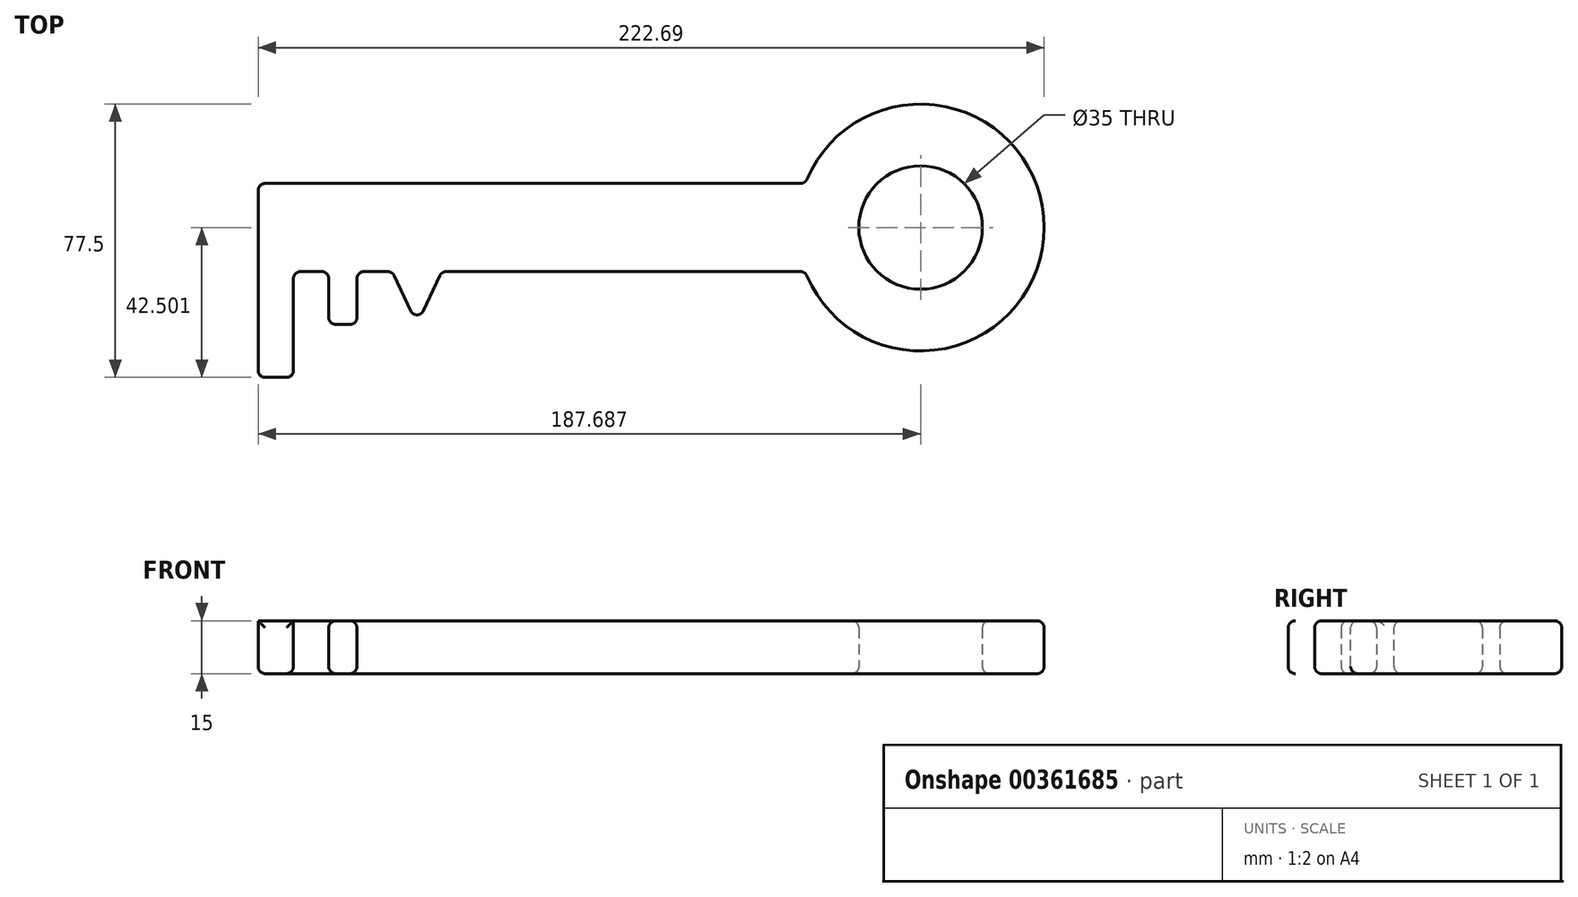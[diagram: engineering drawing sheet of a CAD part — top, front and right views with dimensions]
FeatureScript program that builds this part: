
annotation { "Feature Type Name" : "Feature", "Feature Type Description" : "" }
export const myFeature = defineFeature(function(context is Context, id is Id, definition is map)
    precondition{}
    {
        {
            var Q0;
            Q0=qCreatedBy(makeId("Top.planeOp"),FACE);
            var sketch = newSketch(context, id + "F0", { "sketchPlane" : qUnion([Q0])});
            skLineSegment(sketch, "E0.bottom", {"start": v(-87.43, 22.6) * mm, "end": v(67.57, 22.6) * mm});
            skLineSegment(sketch, "E0.top", {"start": v(-87.43, -2.4) * mm, "end": v(67.57, -2.4) * mm});
            skLineSegment(sketch, "E0.left", {"start": v(-87.43, 22.6) * mm, "end": v(-87.43, -2.4) * mm});
            skLineSegment(sketch, "E0.right", {"start": v(67.57, 22.6) * mm, "end": v(67.57, -2.4) * mm});
            skLineSegment(sketch, "E1.bottom", {"start": v(-87.43, -2.4) * mm, "end": v(-77.43, -2.4) * mm});
            skLineSegment(sketch, "E1.top", {"start": v(-87.43, -32.4) * mm, "end": v(-77.43, -32.4) * mm});
            skLineSegment(sketch, "E1.left", {"start": v(-87.43, -2.4) * mm, "end": v(-87.43, -32.4) * mm});
            skLineSegment(sketch, "E1.right", {"start": v(-77.43, -2.4) * mm, "end": v(-77.43, -32.4) * mm});
            skLineSegment(sketch, "E2.bottom", {"start": v(-67.43, -2.4) * mm, "end": v(-59.43, -2.4) * mm});
            skLineSegment(sketch, "E2.top", {"start": v(-67.43, -17.4) * mm, "end": v(-59.43, -17.4) * mm});
            skLineSegment(sketch, "E2.left", {"start": v(-67.43, -2.4) * mm, "end": v(-67.43, -17.4) * mm});
            skLineSegment(sketch, "E2.right", {"start": v(-59.43, -2.4) * mm, "end": v(-59.43, -17.4) * mm});
            skLineSegment(sketch, "E3", {"start": v(-49.43, -2.4) * mm, "end": v(-42.43, -17.4) * mm});
            skLineSegment(sketch, "E4", {"start": v(-35.43, -2.4) * mm, "end": v(-42.43, -17.4) * mm});
            skArc(sketch, "E5", {"start": v(67.57, -2.4) * mm, "mid": v(135.26, 10.1) * mm, "end": v(67.57, 22.6) * mm});
            skCircle(sketch, "E6", {"center": v(100.26, 10.1) * mm, "radius": 17.5 * mm});
            skLineSegment(sketch, "E7", {"start": v(100.26, 10.1) * mm, "end": v(-87.43, 10.1) * mm, "construction": true});
            skSolve(sketch);
        }
        {
            var Q0;
            Q0 = qSketchRegion(id + "F0", true);
            extrude(context, id + "F1", {"entities" : qUnion([Q0]), "depth" : 15 * mm});
        }
        {
            var Q0;
            Q0=makeQuery(id+"F1.opExtrude","SWEPT_EDGE",EDGE,{"disambiguationData":[OSD([sQuery(id+"F0.wireOp",EDGE,"E0.top"),sQuery(id+"F0.wireOp",EDGE,"E4")])]});
            var Q1;
            Q1=makeQuery(id+"F1.opExtrude","CAP_EDGE",EDGE,{"disambiguationData":[OSD([sQuery(id+"F0.wireOp",EDGE,"E3")])],"isStart":true});
            var Q2;
            Q2=makeQuery(id+"F1.opExtrude","SWEPT_EDGE",EDGE,{"disambiguationData":[OSD([sQuery(id+"F0.wireOp",EDGE,"E2.top"),sQuery(id+"F0.wireOp",EDGE,"E2.right")])]});
            var Q3;
            Q3=makeQuery(id+"F1.opExtrude","SWEPT_EDGE",EDGE,{"disambiguationData":[OSD([sQuery(id+"F0.wireOp",EDGE,"E0.top"),sQuery(id+"F0.wireOp",EDGE,"E3")])]});
            var Q4;
            Q4=makeQuery(id+"F1.opExtrude","SWEPT_EDGE",EDGE,{"disambiguationData":[OSD([sQuery(id+"F0.wireOp",EDGE,"E2.top"),sQuery(id+"F0.wireOp",EDGE,"E2.left")])]});
            var Q5;
            Q5=makeQuery(id+"F1.opExtrude","SWEPT_EDGE",EDGE,{"disambiguationData":[OSD([sQuery(id+"F0.wireOp",EDGE,"E3"),sQuery(id+"F0.wireOp",EDGE,"E4")])]});
            var Q6;
            Q6=makeQuery(id+"F1.opExtrude","CAP_EDGE",EDGE,{"disambiguationData":[OSD([sQuery(id+"F0.wireOp",EDGE,"E3")])],"isStart":false});
            var Q7;
            Q7=makeQuery(id+"F1.opExtrude","CAP_EDGE",EDGE,{"disambiguationData":[OSD([sQuery(id+"F0.wireOp",EDGE,"E4")])],"isStart":true});
            var Q8;
            Q8=makeQuery(id+"F1.opExtrude","CAP_EDGE",EDGE,{"disambiguationData":[OSD([sQuery(id+"F0.wireOp",EDGE,"E0.left"),sQuery(id+"F0.wireOp",EDGE,"E1.left")])],"isStart":true});
            var Q9;
            Q9=makeQuery(id+"F1.opExtrude","CAP_EDGE",EDGE,{"disambiguationData":[OSD([sQuery(id+"F0.wireOp",EDGE,"E5")])],"isStart":true});
            var Q10;
            Q10=makeQuery(id+"F1.opExtrude","CAP_EDGE",EDGE,{"disambiguationData":[OSD([sQuery(id+"F0.wireOp",EDGE,"E5")])],"isStart":false});
            var Q11;
            Q11=makeQuery(id+"F1.opExtrude","CAP_EDGE",EDGE,{"disambiguationData":[OSD([sQuery(id+"F0.wireOp",EDGE,"E6")])],"isStart":true});
            var Q12;
            Q12=makeQuery(id+"F1.opExtrude","CAP_EDGE",EDGE,{"disambiguationData":[OSD([sQuery(id+"F0.wireOp",EDGE,"E6")])],"isStart":false});
            var Q13;
            Q13=makeQuery(id+"F1.opExtrude","CAP_EDGE",EDGE,{"disambiguationData":[OSD([sQuery(id+"F0.wireOp",EDGE,"E1.right")])],"isStart":true});
            var Q14;
            Q14=makeQuery(id+"F1.opExtrude","SWEPT_EDGE",EDGE,{"disambiguationData":[OSD([sQuery(id+"F0.wireOp",EDGE,"E0.bottom"),sQuery(id+"F0.wireOp",EDGE,"E0.left")])]});
            var Q15;
            {var subQ0=sQuery(id+"F0.wireOp",EDGE,"E0.top");Q15=makeQuery(id+"F1.opExtrude","CAP_EDGE",EDGE,{"disambiguationData":[OSD([subQ0]),TDD([makeQuery(id+"F0.imprint","IMPRINT",EDGE,{"disambiguationData":[TD([[makeQuery(id+"F0.imprint","INTERSECT",VERTEX,{"derivedFrom":[subQ0,sQuery(id+"F0.wireOp",EDGE,"E1.bottom"),sQuery(id+"F0.wireOp",EDGE,"E1.right")]}),-1.0]])],"derivedFrom":subQ0})])],"isStart":true});}
            var Q16;
            Q16=makeQuery(id+"F1.opExtrude","SWEPT_EDGE",EDGE,{"disambiguationData":[OSD([sQuery(id+"F0.wireOp",EDGE,"E0.top"),sQuery(id+"F0.wireOp",EDGE,"E2.bottom"),sQuery(id+"F0.wireOp",EDGE,"E2.right")])]});
            var Q17;
            Q17=makeQuery(id+"F1.opExtrude","SWEPT_EDGE",EDGE,{"disambiguationData":[OSD([sQuery(id+"F0.wireOp",EDGE,"E0.top"),sQuery(id+"F0.wireOp",EDGE,"E0.right"),sQuery(id+"F0.wireOp",EDGE,"E5")])]});
            var Q18;
            {var subQ0=sQuery(id+"F0.wireOp",EDGE,"E0.top");Q18=makeQuery(id+"F1.opExtrude","CAP_EDGE",EDGE,{"disambiguationData":[OSD([subQ0]),TDD([makeQuery(id+"F0.imprint","IMPRINT",EDGE,{"disambiguationData":[TD([[makeQuery(id+"F0.imprint","INTERSECT",VERTEX,{"derivedFrom":[subQ0,sQuery(id+"F0.wireOp",EDGE,"E3")]}),1.0]])],"derivedFrom":subQ0})])],"isStart":true});}
            var Q19;
            Q19=makeQuery(id+"F1.opExtrude","CAP_EDGE",EDGE,{"disambiguationData":[OSD([sQuery(id+"F0.wireOp",EDGE,"E0.bottom")])],"isStart":true});
            var Q20;
            Q20=makeQuery(id+"F1.opExtrude","CAP_EDGE",EDGE,{"disambiguationData":[OSD([sQuery(id+"F0.wireOp",EDGE,"E0.bottom")])],"isStart":false});
            var Q21;
            Q21=makeQuery(id+"F1.opExtrude","SWEPT_EDGE",EDGE,{"disambiguationData":[OSD([sQuery(id+"F0.wireOp",EDGE,"E0.bottom"),sQuery(id+"F0.wireOp",EDGE,"E0.right"),sQuery(id+"F0.wireOp",EDGE,"E5")])]});
            var Q22;
            Q22=makeQuery(id+"F1.opExtrude","SWEPT_EDGE",EDGE,{"disambiguationData":[OSD([sQuery(id+"F0.wireOp",EDGE,"E0.top"),sQuery(id+"F0.wireOp",EDGE,"E1.bottom"),sQuery(id+"F0.wireOp",EDGE,"E1.right")])]});
            var Q23;
            Q23=makeQuery(id+"F1.opExtrude","CAP_EDGE",EDGE,{"disambiguationData":[OSD([sQuery(id+"F0.wireOp",EDGE,"E2.right")])],"isStart":false});
            var Q24;
            {var subQ0=sQuery(id+"F0.wireOp",EDGE,"E0.top");Q24=makeQuery(id+"F1.opExtrude","CAP_EDGE",EDGE,{"disambiguationData":[OSD([subQ0]),TDD([makeQuery(id+"F0.imprint","IMPRINT",EDGE,{"disambiguationData":[TD([[makeQuery(id+"F0.imprint","INTERSECT",VERTEX,{"derivedFrom":[subQ0,sQuery(id+"F0.wireOp",EDGE,"E1.bottom"),sQuery(id+"F0.wireOp",EDGE,"E1.right")]}),-1.0]])],"derivedFrom":subQ0})])],"isStart":false});}
            var Q25;
            {var subQ0=sQuery(id+"F0.wireOp",EDGE,"E0.top");Q25=makeQuery(id+"F1.opExtrude","CAP_EDGE",EDGE,{"disambiguationData":[OSD([subQ0]),TDD([makeQuery(id+"F0.imprint","IMPRINT",EDGE,{"disambiguationData":[TD([[makeQuery(id+"F0.imprint","INTERSECT",VERTEX,{"derivedFrom":[subQ0,sQuery(id+"F0.wireOp",EDGE,"E3")]}),1.0]])],"derivedFrom":subQ0})])],"isStart":false});}
            var Q26;
            Q26=makeQuery(id+"F1.opExtrude","CAP_EDGE",EDGE,{"disambiguationData":[OSD([sQuery(id+"F0.wireOp",EDGE,"E2.left")])],"isStart":true});
            var Q27;
            Q27=makeQuery(id+"F1.opExtrude","CAP_EDGE",EDGE,{"disambiguationData":[OSD([sQuery(id+"F0.wireOp",EDGE,"E2.left")])],"isStart":false});
            var Q28;
            Q28=makeQuery(id+"F1.opExtrude","CAP_EDGE",EDGE,{"disambiguationData":[OSD([sQuery(id+"F0.wireOp",EDGE,"E2.right")])],"isStart":true});
            var Q29;
            {var subQ0=sQuery(id+"F0.wireOp",EDGE,"E0.top");Q29=makeQuery(id+"F1.opExtrude","CAP_EDGE",EDGE,{"disambiguationData":[OSD([subQ0]),TDD([makeQuery(id+"F0.imprint","IMPRINT",EDGE,{"disambiguationData":[TD([[makeQuery(id+"F0.imprint","INTERSECT",VERTEX,{"derivedFrom":[subQ0,sQuery(id+"F0.wireOp",EDGE,"E4")]}),-1.0]])],"derivedFrom":subQ0})])],"isStart":true});}
            var Q30;
            {var subQ0=sQuery(id+"F0.wireOp",EDGE,"E0.top");Q30=makeQuery(id+"F1.opExtrude","CAP_EDGE",EDGE,{"disambiguationData":[OSD([subQ0]),TDD([makeQuery(id+"F0.imprint","IMPRINT",EDGE,{"disambiguationData":[TD([[makeQuery(id+"F0.imprint","INTERSECT",VERTEX,{"derivedFrom":[subQ0,sQuery(id+"F0.wireOp",EDGE,"E4")]}),-1.0]])],"derivedFrom":subQ0})])],"isStart":false});}
            var Q31;
            Q31=makeQuery(id+"F1.opExtrude","CAP_EDGE",EDGE,{"disambiguationData":[OSD([sQuery(id+"F0.wireOp",EDGE,"E4")])],"isStart":false});
            var Q32;
            Q32=makeQuery(id+"F1.opExtrude","CAP_EDGE",EDGE,{"disambiguationData":[OSD([sQuery(id+"F0.wireOp",EDGE,"E1.top")])],"isStart":true});
            var Q33;
            Q33=makeQuery(id+"F1.opExtrude","CAP_EDGE",EDGE,{"disambiguationData":[OSD([sQuery(id+"F0.wireOp",EDGE,"E2.top")])],"isStart":true});
            var Q34;
            Q34=makeQuery(id+"F1.opExtrude","CAP_EDGE",EDGE,{"disambiguationData":[OSD([sQuery(id+"F0.wireOp",EDGE,"E2.top")])],"isStart":false});
            var Q35;
            Q35=makeQuery(id+"F1.opExtrude","SWEPT_EDGE",EDGE,{"disambiguationData":[OSD([sQuery(id+"F0.wireOp",EDGE,"E0.top"),sQuery(id+"F0.wireOp",EDGE,"E2.bottom"),sQuery(id+"F0.wireOp",EDGE,"E2.left")])]});
            var Q36;
            Q36=makeQuery(id+"F1.opExtrude","SWEPT_EDGE",EDGE,{"disambiguationData":[OSD([sQuery(id+"F0.wireOp",EDGE,"E1.top"),sQuery(id+"F0.wireOp",EDGE,"E1.left")])]});
            var Q37;
            Q37=makeQuery(id+"F1.opExtrude","CAP_EDGE",EDGE,{"disambiguationData":[OSD([sQuery(id+"F0.wireOp",EDGE,"E1.top")])],"isStart":false});
            var Q38;
            Q38=makeQuery(id+"F1.opExtrude","SWEPT_EDGE",EDGE,{"disambiguationData":[OSD([sQuery(id+"F0.wireOp",EDGE,"E1.top"),sQuery(id+"F0.wireOp",EDGE,"E1.right")])]});
            fillet(context, id + "F2", {"entities" : qUnion([Q0, Q1, Q2, Q3, Q4, Q5, Q6, Q7, Q8, Q9, Q10, Q11, Q12, Q13, Q14, Q15, Q16, Q17, Q18, Q19, Q20, Q21, Q22, Q23, Q24, Q25, Q26, Q27, Q28, Q29, Q30, Q31, Q32, Q33, Q34, Q35, Q36, Q37, Q38]), "radius" : 2 * mm, "tangentPropagation" : true, "allowEdgeOverflow" : false});
        }
    });
